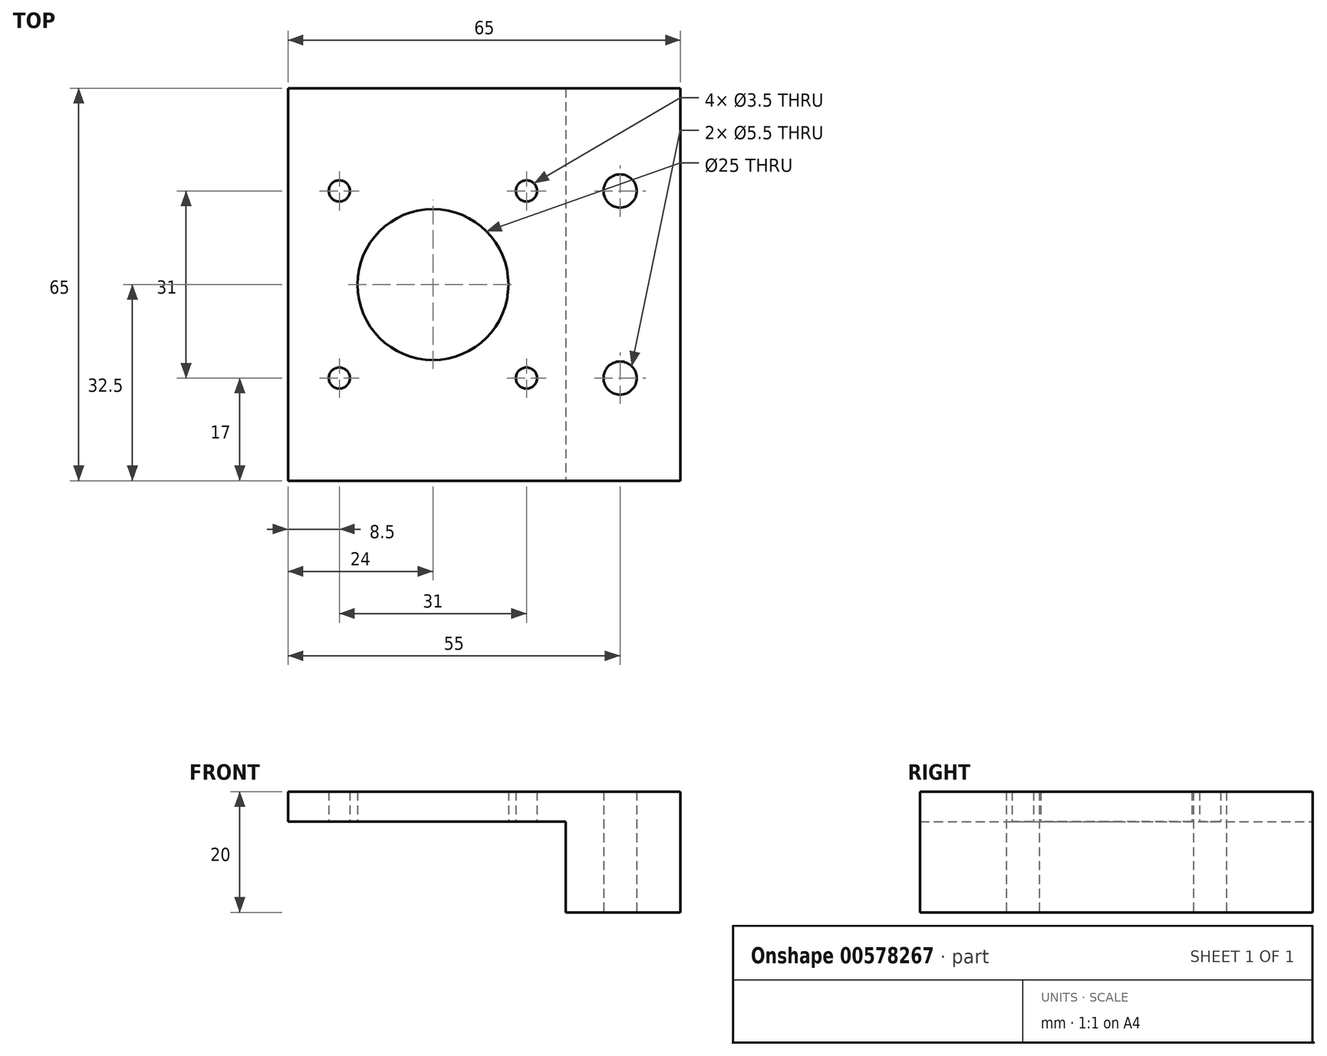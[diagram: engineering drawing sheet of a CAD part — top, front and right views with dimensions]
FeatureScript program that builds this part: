
annotation { "Feature Type Name" : "Feature", "Feature Type Description" : "" }
export const myFeature = defineFeature(function(context is Context, id is Id, definition is map)
    precondition{}
    {
        {
            var Q0;
            Q0=qCreatedBy(makeId("Top.planeOp"),FACE);
            var sketch = newSketch(context, id + "F0", { "sketchPlane" : qUnion([Q0])});
            skCircle(sketch, "E0", {"center": v(-10, 48) * mm, "radius": 2.75 * mm});
            skCircle(sketch, "E1", {"center": v(-10, 17) * mm, "radius": 2.75 * mm});
            skCircle(sketch, "E2", {"center": v(-41, 32.5) * mm, "radius": 12.5 * mm});
            skLineSegment(sketch, "E3", {"start": v(0, 0) * mm, "end": v(-65, 0) * mm});
            skLineSegment(sketch, "E4", {"start": v(-65, 0) * mm, "end": v(-65, 65) * mm});
            skLineSegment(sketch, "E5", {"start": v(-65, 65) * mm, "end": v(0, 65) * mm});
            skLineSegment(sketch, "E6", {"start": v(0, 65) * mm, "end": v(0, 0) * mm});
            skLineSegment(sketch, "E7", {"start": v(-19, 65) * mm, "end": v(-19, 0) * mm});
            skCircle(sketch, "E8", {"center": v(-25.5, 48) * mm, "radius": 1.75 * mm});
            skCircle(sketch, "E9", {"center": v(-56.5, 48) * mm, "radius": 1.75 * mm});
            skCircle(sketch, "E10", {"center": v(-25.5, 17) * mm, "radius": 1.75 * mm});
            skCircle(sketch, "E11", {"center": v(-56.5, 17) * mm, "radius": 1.75 * mm});
            skSolve(sketch);
        }
        {
            var Q0;
            Q0=qSketchRegion(id+"F0",true);
            extrude(context, id + "F1", {"entities" : qUnion([Q0]), "depth" : 20 * mm, "offsetDistance" : 25 * mm});
        }
        {
            var Q0;
            Q0=makeQuery(id+"F0.imprint","IMPRINT",FACE,{"disambiguationData":[TD([[makeQuery(id+"F0.imprint","IMPRINT",EDGE,{"derivedFrom":sQuery(id+"F0.wireOp",EDGE,"E2")}),-1.0]])]});
            extrude(context, id + "F2", {"entities" : qUnion([Q0]), "operationType" : NewBodyOperationType.REMOVE, "depth" : 15 * mm, "offsetDistance" : 25 * mm});
        }
    });
